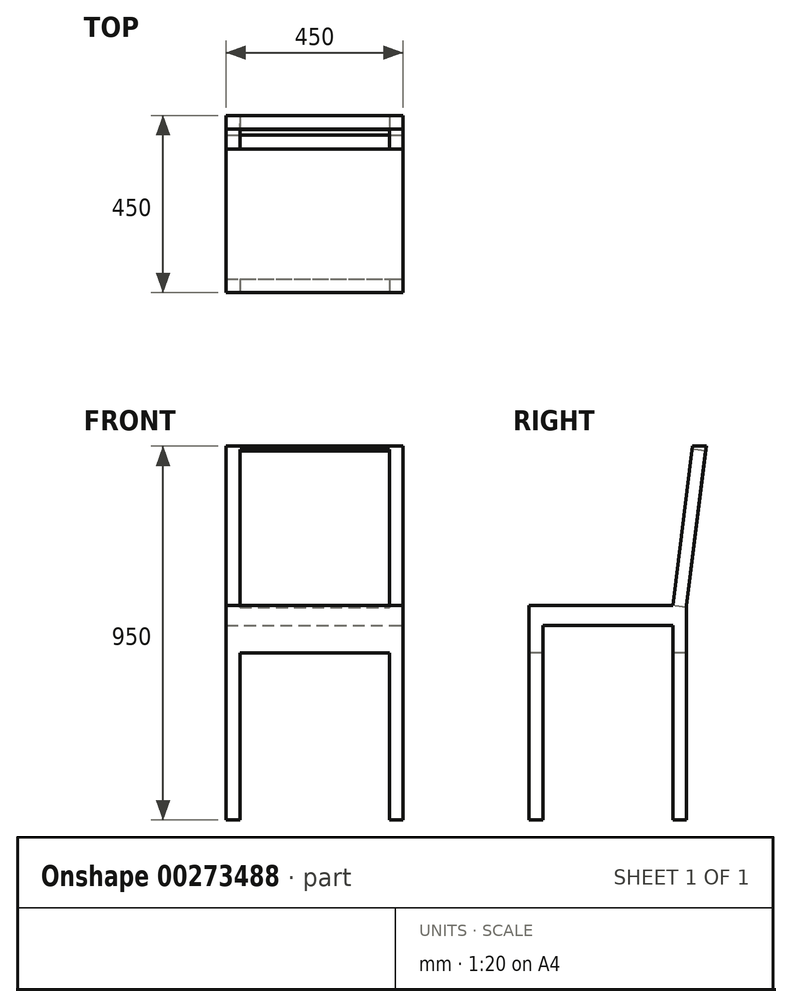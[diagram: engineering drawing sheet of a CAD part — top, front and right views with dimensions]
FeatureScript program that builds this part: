
annotation { "Feature Type Name" : "Feature", "Feature Type Description" : "" }
export const myFeature = defineFeature(function(context is Context, id is Id, definition is map)
    precondition{}
    {
        {
            var Q0;
            Q0=qCreatedBy(makeId("Top.planeOp"),FACE);
            var sketch = newSketch(context, id + "F0", { "sketchPlane" : qUnion([Q0])});
            skLineSegment(sketch, "E0.bottom", {"start": v(225, 225) * mm, "end": v(-225, 225) * mm});
            skLineSegment(sketch, "E0.top", {"start": v(225, -225) * mm, "end": v(-225, -225) * mm});
            skLineSegment(sketch, "E0.left", {"start": v(225, 225) * mm, "end": v(225, -225) * mm});
            skLineSegment(sketch, "E0.right", {"start": v(-225, 225) * mm, "end": v(-225, -225) * mm});
            skPoint(sketch, "E0.middle", {"position": v(0, 0) * mm});
            skSolve(sketch);
        }
        {
            var Q0;
            Q0=qSketchRegion(id+"F0",true);
            extrude(context, id + "F1", {"entities" : qUnion([Q0]), "depth" : 950 * mm});
        }
        {
            var Q0;
            Q0=makeQuery(id+"F1.opExtrude","SWEPT_FACE",FACE,{"disambiguationData":[OSD([sQuery(id+"F0.wireOp",EDGE,"E0.left")])]});
            var sketch = newSketch(context, id + "F2", { "sketchPlane" : qUnion([Q0])});
            skLineSegment(sketch, "E1.bottom", {"start": v(-225, 544.97) * mm, "end": v(225, 544.97) * mm});
            skLineSegment(sketch, "E1.top", {"start": v(-225, 494.97) * mm, "end": v(225, 494.97) * mm});
            skLineSegment(sketch, "E1.left", {"start": v(-225, 544.97) * mm, "end": v(-225, 494.97) * mm});
            skLineSegment(sketch, "E1.right", {"start": v(225, 544.97) * mm, "end": v(225, 494.97) * mm});
            skLineSegment(sketch, "E2", {"start": v(225, 950) * mm, "end": v(175, 544.97) * mm});
            skLineSegment(sketch, "E3", {"start": v(190, 950) * mm, "end": v(140, 544.97) * mm});
            skLineSegment(sketch, "E4", {"start": v(140, 544.97) * mm, "end": v(140, 0) * mm});
            skLineSegment(sketch, "E5", {"start": v(175, 544.97) * mm, "end": v(175, 0) * mm});
            skLineSegment(sketch, "E6", {"start": v(-190, 494.97) * mm, "end": v(-190, 0) * mm});
            skSolve(sketch);
        }
        {
            var Q0;
            {var subQ0=sQuery(id+"F2.wireOp",EDGE,"E6");Q0=makeQuery(id+"F2.imprint","IMPRINT",FACE,{"disambiguationData":[TD([[makeQuery(id+"F2.imprint","IMPRINT",EDGE,{"derivedFrom":subQ0}),1.0]])]});}
            var Q1;
            {var subQ1=sQuery(id+"F0.wireOp",EDGE,"E0.left");var subQ4=sQuery(id+"F2.wireOp",EDGE,"E5");var subQ6=makeQuery(id+"F1.opExtrude","CAP_EDGE",EDGE,{"disambiguationData":[OSD([subQ1])],"isStart":true});var subQ7=makeQuery(id+"F2.imprint","INTERSECT",VERTEX,{"derivedFrom":[subQ6,subQ4]});Q1=makeQuery(id+"F2.imprint","IMPRINT",FACE,{"disambiguationData":[TD([[makeQuery(id+"F2.imprint","IMPRINT",EDGE,{"disambiguationData":[TD([[subQ7,1.0]])],"derivedFrom":subQ4}),1.0]])]});}
            var Q2;
            {var subQ4=sQuery(id+"F2.wireOp",EDGE,"E2");Q2=makeQuery(id+"F2.imprint","IMPRINT",FACE,{"disambiguationData":[TD([[makeQuery(id+"F2.imprint","IMPRINT",EDGE,{"derivedFrom":subQ4}),1.0]])]});}
            var Q3;
            {var subQ0=sQuery(id+"F2.wireOp",EDGE,"E1.right");Q3=makeQuery(id+"F2.imprint","IMPRINT",FACE,{"disambiguationData":[TD([[makeQuery(id+"F2.imprint","IMPRINT",EDGE,{"derivedFrom":subQ0}),-1.0]])]});}
            var Q4;
            {var subQ4=sQuery(id+"F2.wireOp",EDGE,"E3");Q4=makeQuery(id+"F2.imprint","IMPRINT",FACE,{"disambiguationData":[TD([[makeQuery(id+"F2.imprint","IMPRINT",EDGE,{"derivedFrom":subQ4}),-1.0]])]});}
            extrude(context, id + "F3", {"entities" : qUnion([Q0, Q1, Q2, Q3, Q4]), "operationType" : NewBodyOperationType.REMOVE, "endBound" : BoundingType.THROUGH_ALL, "oppositeDirection" : true, "depth" : 25 * mm});
        }
        {
            var Q0;
            Q0=makeQuery(id+"F1.opExtrude","SWEPT_FACE",FACE,{"disambiguationData":[OSD([sQuery(id+"F0.wireOp",EDGE,"E0.top")])]});
            var sketch = newSketch(context, id + "F4", { "sketchPlane" : qUnion([Q0])});
            skLineSegment(sketch, "E7.bottom", {"start": v(-190, 425) * mm, "end": v(190, 425) * mm});
            skLineSegment(sketch, "E7.top", {"start": v(-190, 0) * mm, "end": v(190, 0) * mm});
            skLineSegment(sketch, "E7.left", {"start": v(-190, 425) * mm, "end": v(-190, 0) * mm});
            skLineSegment(sketch, "E7.right", {"start": v(190, 425) * mm, "end": v(190, 0) * mm});
            skSolve(sketch);
        }
        {
            var Q0;
            Q0 = qSketchRegion(id + "F4", true);
            extrude(context, id + "F5", {"entities" : qUnion([Q0]), "operationType" : NewBodyOperationType.REMOVE, "endBound" : BoundingType.THROUGH_ALL, "oppositeDirection" : true, "depth" : 25 * mm});
        }
        {
            var Q0;
            Q0=makeQuery(id+"F3.boolean.opBoolean","COPY",FACE,{"derivedFrom":makeQuery(id+"F3.opExtrude","SWEPT_FACE",FACE,{"disambiguationData":[OSD([sQuery(id+"F2.wireOp",EDGE,"E3")])]})});
            var sketch = newSketch(context, id + "F6", { "sketchPlane" : qUnion([Q0])});
            skLineSegment(sketch, "E8", {"start": v(-190, 558.02) * mm, "end": v(-190, 958.02) * mm});
            skLineSegment(sketch, "E9", {"start": v(-190, 958.02) * mm, "end": v(190, 958.02) * mm});
            skLineSegment(sketch, "E10", {"start": v(190, 958.02) * mm, "end": v(190, 558.02) * mm});
            skLineSegment(sketch, "E11.top", {"start": v(-190, 883.02) * mm, "end": v(190, 883.02) * mm});
            skLineSegment(sketch, "E11.left", {"start": v(-190, 958.02) * mm, "end": v(-190, 883.02) * mm});
            skLineSegment(sketch, "E11.right", {"start": v(190, 958.02) * mm, "end": v(190, 883.02) * mm});
            skLineSegment(sketch, "E12.top", {"start": v(-190, 833.02) * mm, "end": v(190, 833.02) * mm});
            skLineSegment(sketch, "E12.left", {"start": v(-190, 883.02) * mm, "end": v(-190, 833.02) * mm});
            skLineSegment(sketch, "E12.right", {"start": v(190, 883.02) * mm, "end": v(190, 833.02) * mm});
            skSolve(sketch);
        }
        {
            var Q0;
            {var subQ0=sQuery(id+"F6.wireOp",EDGE,"E8");Q0=makeQuery(id+"F6.imprint","IMPRINT",FACE,{"disambiguationData":[TD([[makeQuery(id+"F6.imprint","IMPRINT",EDGE,{"derivedFrom":subQ0}),-1.0]])]});}
            var Q1;
            Q1=makeQuery(id+"F6.imprint","IMPRINT",FACE,{"disambiguationData":[TD([[makeQuery(id+"F6.imprint","IMPRINT",EDGE,{"derivedFrom":sQuery(id+"F6.wireOp",EDGE,"E9")}),-1.0]])]});
            extrude(context, id + "F7", {"entities" : qUnion([Q0, Q1]), "operationType" : NewBodyOperationType.REMOVE, "endBound" : BoundingType.THROUGH_ALL, "oppositeDirection" : true, "depth" : 25 * mm});
        }
    });
